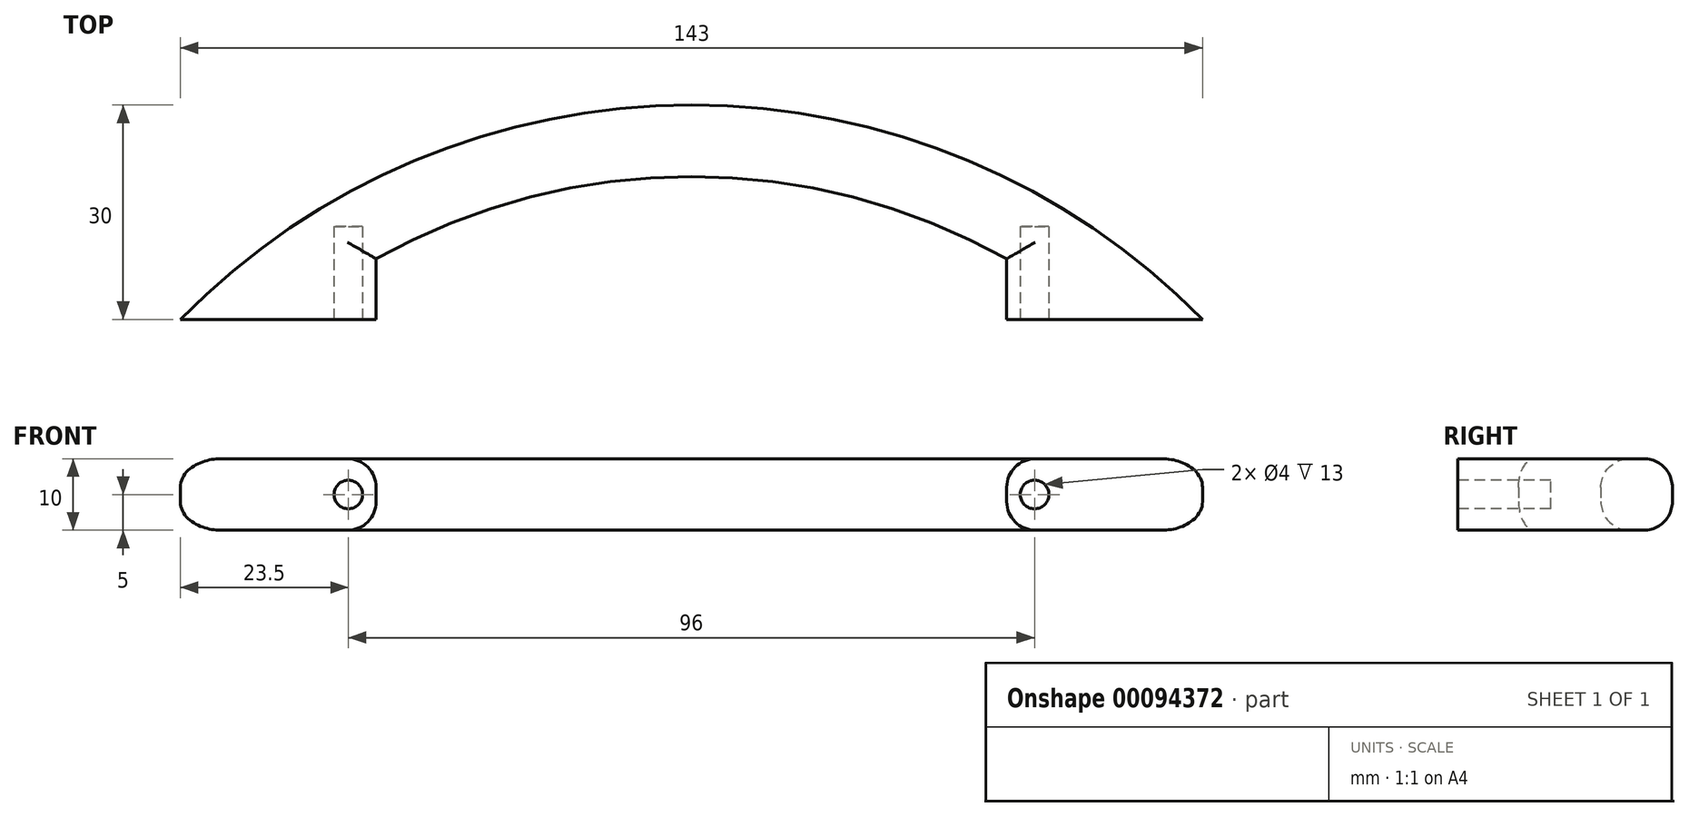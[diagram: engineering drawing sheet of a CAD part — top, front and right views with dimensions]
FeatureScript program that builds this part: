
annotation { "Feature Type Name" : "Feature", "Feature Type Description" : "" }
export const myFeature = defineFeature(function(context is Context, id is Id, definition is map)
    precondition{}
    {
        {
            var Q0;
            Q0=qCreatedBy(makeId("Top.planeOp"),FACE);
            var sketch = newSketch(context, id + "F0", { "sketchPlane" : qUnion([Q0])});
            skArc(sketch, "E0", {"start": v(71.5, 0) * mm, "mid": v(0, 30) * mm, "end": v(-71.5, 0) * mm});
            skArc(sketch, "E1.0", {"start": v(44.1, 8.48) * mm, "mid": v(0, 20) * mm, "end": v(-44.1, 8.48) * mm});
            skLineSegment(sketch, "E2", {"start": v(-71.5, 0) * mm, "end": v(-44.1, 0) * mm});
            skLineSegment(sketch, "E3", {"start": v(-44.1, 0) * mm, "end": v(-44.1, 8.48) * mm});
            skLineSegment(sketch, "E4", {"start": v(71.5, 0) * mm, "end": v(44.1, 0) * mm});
            skLineSegment(sketch, "E5", {"start": v(44.1, 0) * mm, "end": v(44.1, 8.48) * mm});
            skSolve(sketch);
        }
        {
            var Q0;
            Q0=makeQuery(id+"F0.imprint","IMPRINT",FACE,{"disambiguationData":[TD([[makeQuery(id+"F0.imprint","IMPRINT",EDGE,{"derivedFrom":sQuery(id+"F0.wireOp",EDGE,"E0")}),1.0]])]});
            extrude(context, id + "F1", {"entities" : qUnion([Q0]), "depth" : 10 * mm});
        }
        {
            var Q0;
            Q0=makeQuery(id+"F1.opExtrude","CAP_EDGE",EDGE,{"disambiguationData":[OSD([sQuery(id+"F0.wireOp",EDGE,"E1.0")])],"isStart":false});
            var Q1;
            Q1=makeQuery(id+"F1.opExtrude","CAP_EDGE",EDGE,{"disambiguationData":[OSD([sQuery(id+"F0.wireOp",EDGE,"E0")])],"isStart":false});
            var Q2;
            Q2=makeQuery(id+"F1.opExtrude","CAP_EDGE",EDGE,{"disambiguationData":[OSD([sQuery(id+"F0.wireOp",EDGE,"E1.0")])],"isStart":true});
            var Q3;
            Q3=makeQuery(id+"F1.opExtrude","CAP_EDGE",EDGE,{"disambiguationData":[OSD([sQuery(id+"F0.wireOp",EDGE,"E0")])],"isStart":true});
            var Q4;
            Q4=makeQuery(id+"F1.opExtrude","CAP_EDGE",EDGE,{"disambiguationData":[OSD([sQuery(id+"F0.wireOp",EDGE,"E3")])],"isStart":true});
            var Q5;
            Q5=makeQuery(id+"F1.opExtrude","CAP_EDGE",EDGE,{"disambiguationData":[OSD([sQuery(id+"F0.wireOp",EDGE,"E3")])],"isStart":false});
            var Q6;
            Q6=makeQuery(id+"F1.opExtrude","CAP_EDGE",EDGE,{"disambiguationData":[OSD([sQuery(id+"F0.wireOp",EDGE,"E5")])],"isStart":true});
            var Q7;
            Q7=makeQuery(id+"F1.opExtrude","CAP_EDGE",EDGE,{"disambiguationData":[OSD([sQuery(id+"F0.wireOp",EDGE,"E5")])],"isStart":false});
            fillet(context, id + "F2", {"entities" : qUnion([Q0, Q1, Q2, Q3, Q4, Q5, Q6, Q7]), "radius" : 4 * mm, "tangentPropagation" : true, "allowEdgeOverflow" : false});
        }
        {
            var Q0;
            Q0=makeQuery(id+"F1.opExtrude","SWEPT_FACE",FACE,{"disambiguationData":[OSD([sQuery(id+"F0.wireOp",EDGE,"E4")])]});
            var sketch = newSketch(context, id + "F3", { "sketchPlane" : qUnion([Q0])});
            skCircle(sketch, "E6", {"center": v(48, 5) * mm, "radius": 2 * mm});
            skCircle(sketch, "E7", {"center": v(-48, 5) * mm, "radius": 2 * mm});
            skLineSegment(sketch, "E8", {"start": v(48, 5) * mm, "end": v(44.1, 5) * mm, "construction": true});
            skLineSegment(sketch, "E9", {"start": v(-48, 5) * mm, "end": v(-44.1, 5) * mm, "construction": true});
            skSolve(sketch);
        }
        {
            var Q0;
            Q0=qSketchRegion(id+"F3",true);
            extrude(context, id + "F4", {"entities" : qUnion([Q0]), "operationType" : NewBodyOperationType.REMOVE, "oppositeDirection" : true, "depth" : 13 * mm});
        }
    });
